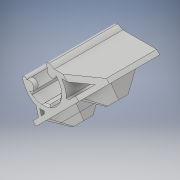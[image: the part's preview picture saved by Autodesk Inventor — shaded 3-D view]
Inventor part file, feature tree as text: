
AUTODESK INVENTOR PART (.ipt)
format: ipt  version: 2017 (Build 210142000, 142)  size: 1,042,944 bytes
history: native  units: in
note: dims shown in document units (in); Inventor stores cm internally (conversion verified against a paired STEP export)
features: other x2, extrude x2, sketch x2
ambient origin geometry x8: Origin, YZ Plane, XZ Plane, XY Plane, X Axis, Y Axis, Z Axis, Center Point
bodies: Solid1 (feature_tree)
feature tree (6):
  other  "10_Support plateau.STEP"
  extrude  "Extrusion1"  Depth=0.3937in TaperAngle=0.0deg
  extrude  "Extrusion2"  [1 undecoded]
  sketch  "Sketch1"  dims[d0=0.3937in d1=0.0in d2=0.3937in d3=0.0in]
  sketch  "Sketch2"
  parser-record x1  (decoder bookkeeping rows leaked as tree rows — omitted from the tree; the rows remain in map.json)
note: 1 required parameter value undecoded (feature->parameter linkage not recoverable at this tier; creation-order binding heuristic only, values carry confidence <= 0.55)
